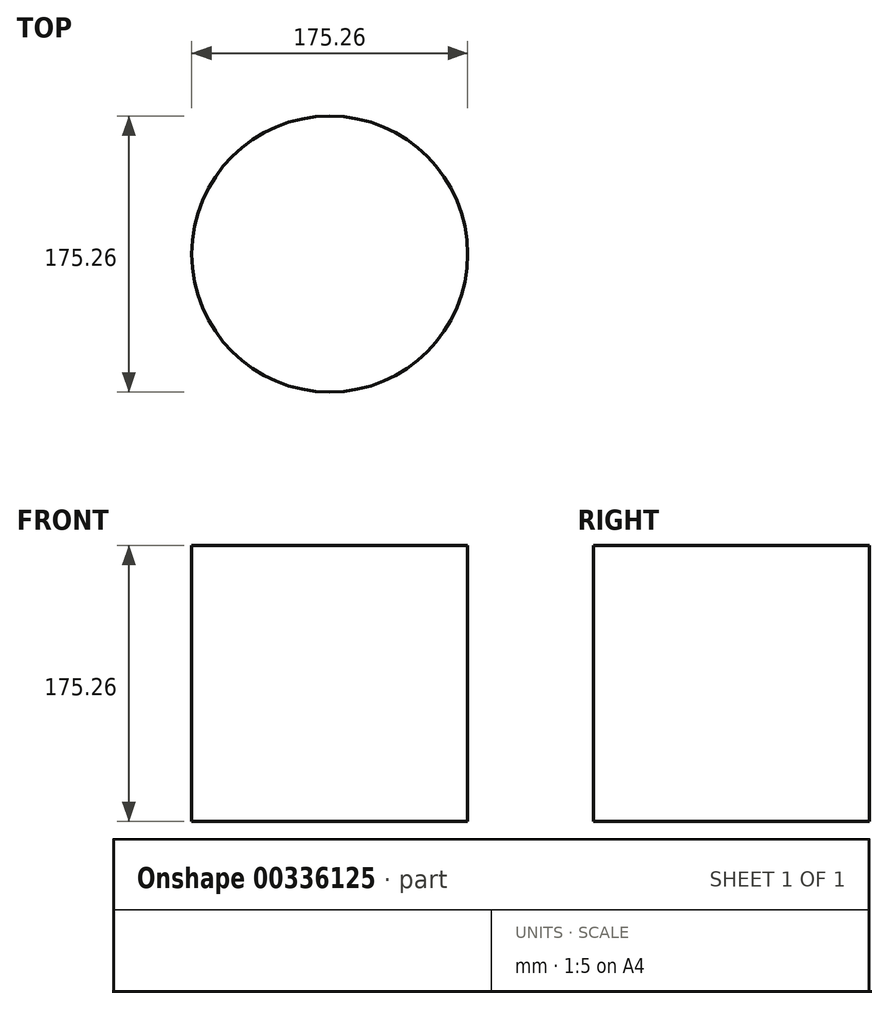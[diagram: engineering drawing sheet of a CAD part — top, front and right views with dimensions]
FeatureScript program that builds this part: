
annotation { "Feature Type Name" : "Feature", "Feature Type Description" : "" }
export const myFeature = defineFeature(function(context is Context, id is Id, definition is map)
    precondition{}
    {
        {
            var Q0;
            Q0=qCreatedBy(makeId("Top.planeOp"),FACE);
            var sketch = newSketch(context, id + "F0", { "sketchPlane" : qUnion([Q0])});
            skCircle(sketch, "E0", {"center": v(-128.94, 43.83) * mm, "radius": 87.63 * mm});
            skSolve(sketch);
        }
        {
            var Q0;
            Q0=makeQuery(id+"F0.imprint","IMPRINT",FACE,{"disambiguationData":[TD([[makeQuery(id+"F0.imprint","IMPRINT",EDGE,{"derivedFrom":sQuery(id+"F0.wireOp",EDGE,"E0")}),1.0]])]});
            extrude(context, id + "F1", {"entities" : qUnion([Q0]), "depth" : 175.26 * mm});
        }
    });
